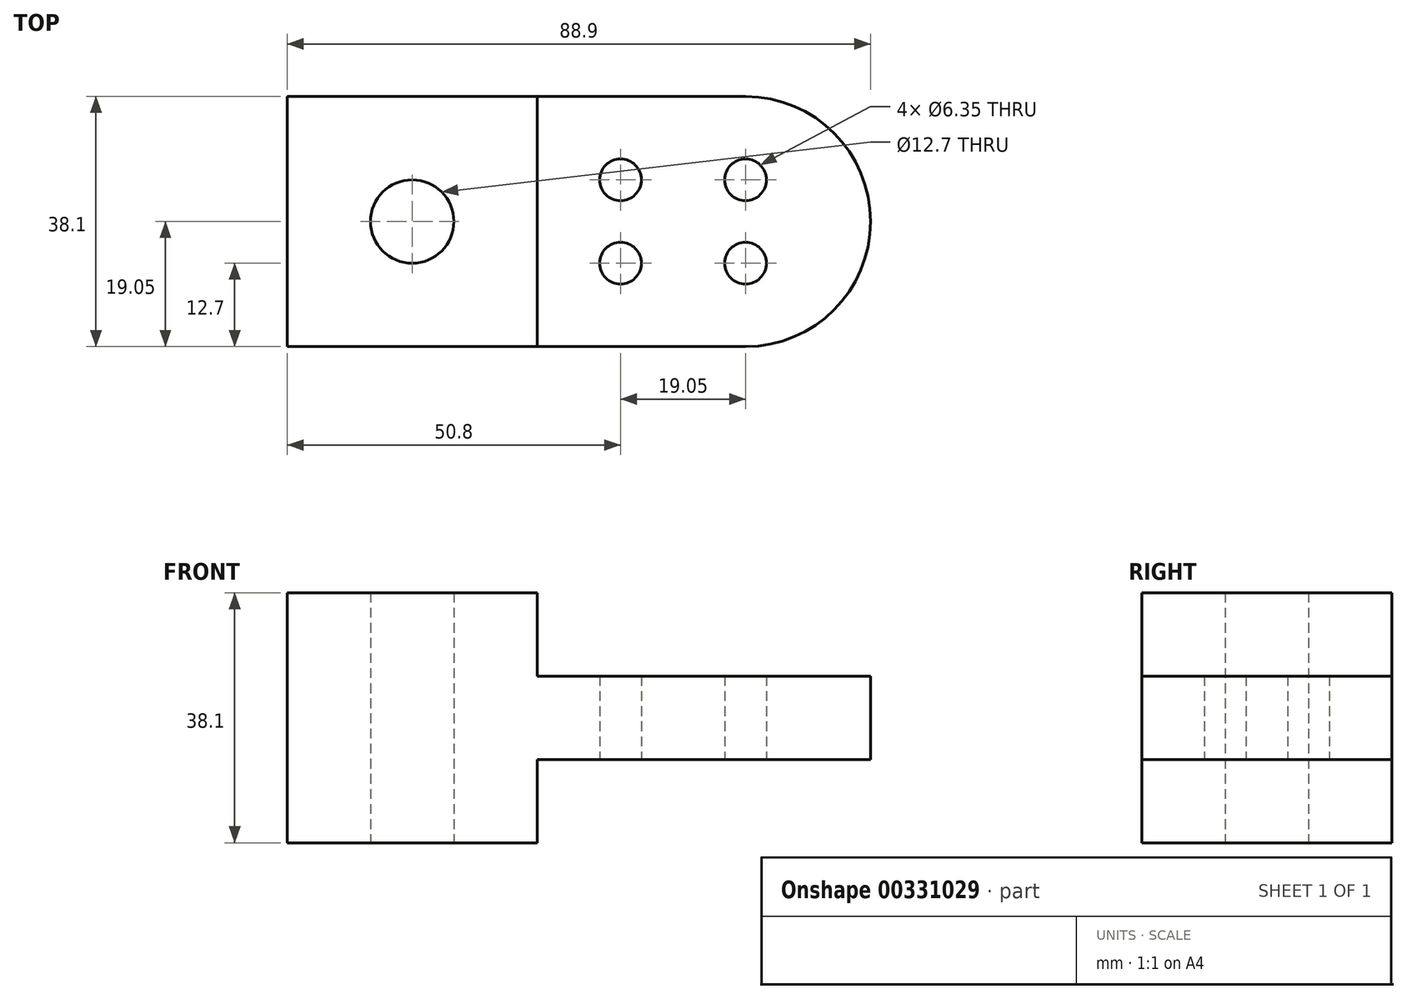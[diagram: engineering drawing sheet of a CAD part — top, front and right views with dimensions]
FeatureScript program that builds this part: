
annotation { "Feature Type Name" : "Feature", "Feature Type Description" : "" }
export const myFeature = defineFeature(function(context is Context, id is Id, definition is map)
    precondition{}
    {
        {
            var Q0;
            Q0=qCreatedBy(makeId("Top.planeOp"),FACE);
            var sketch = newSketch(context, id + "F0", { "sketchPlane" : qUnion([Q0])});
            skLineSegment(sketch, "E0.bottom", {"start": v(0, 0) * mm, "end": v(38.1, 0) * mm});
            skLineSegment(sketch, "E0.top", {"start": v(0, 38.1) * mm, "end": v(38.1, 38.1) * mm});
            skLineSegment(sketch, "E0.left", {"start": v(0, 0) * mm, "end": v(0, 38.1) * mm});
            skLineSegment(sketch, "E0.right", {"start": v(38.1, 0) * mm, "end": v(38.1, 38.1) * mm});
            skCircle(sketch, "E1", {"center": v(19.05, 19.05) * mm, "radius": 6.35 * mm});
            skPoint(sketch, "E1.centerSnap0", {"position": v(0, 19.05) * mm});
            skPoint(sketch, "E1.centerSnap1", {"position": v(19.05, 38.1) * mm});
            skSolve(sketch);
        }
        {
            var Q0;
            Q0 = qSketchRegion(id + "F0", true);
            extrude(context, id + "F1", {"entities" : qUnion([Q0]), "depth" : 25.4 * mm});
        }
        {
            var Q0;
            Q0=makeQuery(id+"F1.opExtrude","CAP_FACE",FACE,{"disambiguationData":[OSD([sQuery(id+"F0.wireOp",EDGE,"E0.bottom"),sQuery(id+"F0.wireOp",EDGE,"E0.top"),sQuery(id+"F0.wireOp",EDGE,"E0.left"),sQuery(id+"F0.wireOp",EDGE,"E0.right"),sQuery(id+"F0.wireOp",EDGE,"E1")])],"isStart":true});
            var sketch = newSketch(context, id + "F2", { "sketchPlane" : qUnion([Q0])});
            skLineSegment(sketch, "E2", {"start": v(38.1, 0) * mm, "end": v(69.85, 0) * mm});
            skLineSegment(sketch, "E3", {"start": v(38.1, -38.1) * mm, "end": v(69.85, -38.1) * mm});
            skArc(sketch, "E4", {"start": v(69.85, -38.1) * mm, "mid": v(88.9, -19.05) * mm, "end": v(69.85, 0) * mm});
            skCircle(sketch, "E5", {"center": v(69.85, -12.7) * mm, "radius": 3.18 * mm});
            skLineSegment(sketch, "E6", {"start": v(69.85, -19.05) * mm, "end": v(38.1, -19.05) * mm, "construction": true});
            skCircle(sketch, "E7.MirrorC", {"center": v(69.85, -25.4) * mm, "radius": 3.18 * mm});
            skCircle(sketch, "E8", {"center": v(50.8, -12.7) * mm, "radius": 3.18 * mm});
            skCircle(sketch, "E9", {"center": v(50.8, -25.4) * mm, "radius": 3.18 * mm});
            skLineSegment(sketch, "E10", {"start": v(38.1, 0) * mm, "end": v(38.1, -38.1) * mm});
            skSolve(sketch);
        }
        {
            var Q0;
            Q0 = qSketchRegion(id + "F2", true);
            extrude(context, id + "F3", {"entities" : qUnion([Q0]), "operationType" : NewBodyOperationType.ADD, "oppositeDirection" : true, "depth" : 12.7 * mm});
        }
        {
            var Q0;
            Q0 = qSketchRegion(id + "F0", true);
            extrude(context, id + "F4", {"entities" : qUnion([Q0]), "operationType" : NewBodyOperationType.ADD, "oppositeDirection" : true, "depth" : 12.7 * mm});
        }
    });
